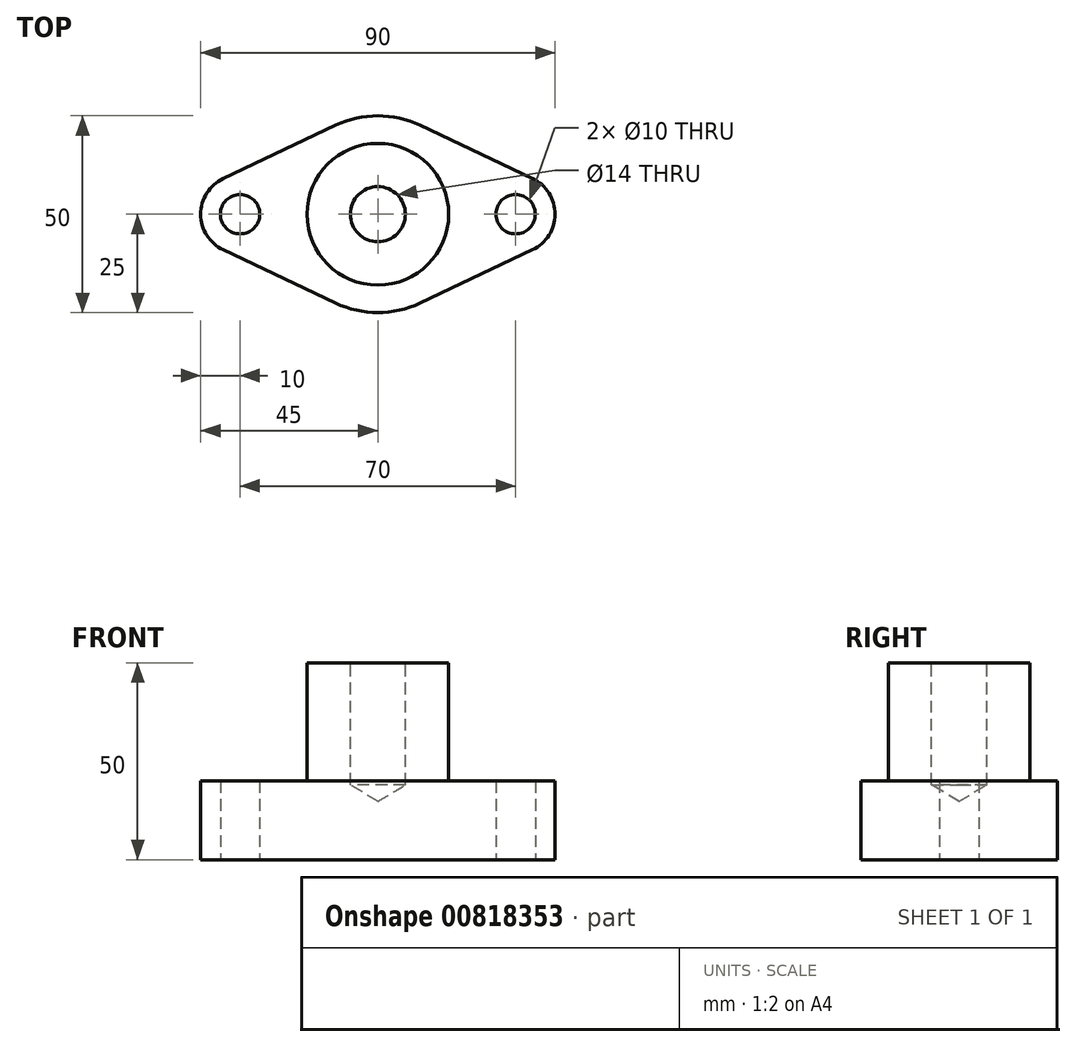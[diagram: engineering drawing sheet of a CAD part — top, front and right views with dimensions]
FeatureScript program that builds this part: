
annotation { "Feature Type Name" : "Feature", "Feature Type Description" : "" }
export const myFeature = defineFeature(function(context is Context, id is Id, definition is map)
    precondition{}
    {
        {
            var Q0;
            Q0=qCreatedBy(makeId("Top.planeOp"),FACE);
            var sketch = newSketch(context, id + "F0", { "sketchPlane" : qUnion([Q0])});
            skLineSegment(sketch, "E0", {"start": v(10.71, 22.59) * mm, "end": v(39.29, 9.04) * mm});
            skLineSegment(sketch, "E1", {"start": v(-39.29, 9.04) * mm, "end": v(-10.71, 22.59) * mm});
            skLineSegment(sketch, "E2", {"start": v(-39.29, -9.04) * mm, "end": v(-10.71, -22.59) * mm});
            skLineSegment(sketch, "E3", {"start": v(10.71, -22.59) * mm, "end": v(39.29, -9.04) * mm});
            skLineSegment(sketch, "E4", {"start": v(-10.71, 22.59) * mm, "end": v(-10.71, 22.59) * mm});
            skArc(sketch, "E5", {"start": v(-10.71, -22.59) * mm, "mid": v(0, -25) * mm, "end": v(10.71, -22.59) * mm});
            skArc(sketch, "E6", {"start": v(10.71, 22.59) * mm, "mid": v(0, 25) * mm, "end": v(-10.71, 22.59) * mm});
            skArc(sketch, "E7", {"start": v(-39.29, 9.04) * mm, "mid": v(-45, 0) * mm, "end": v(-39.29, -9.04) * mm});
            skArc(sketch, "E8", {"start": v(39.29, -9.04) * mm, "mid": v(45, 0) * mm, "end": v(39.29, 9.04) * mm});
            skSolve(sketch);
        }
        {
            var Q0;
            Q0=makeQuery(id+"F0.imprint","IMPRINT",FACE,{"disambiguationData":[TD([[makeQuery(id+"F0.imprint","IMPRINT",EDGE,{"derivedFrom":sQuery(id+"F0.wireOp",EDGE,"E0")}),-1.0]])]});
            extrude(context, id + "F1", {"entities" : qUnion([Q0]), "depth" : 20 * mm, "offsetDistance" : 25 * mm});
        }
        {
            var Q0;
            Q0=sQuery(id+"F0.wireOp",VERTEX,"E7.center");
            var Q1;
            Q1=sQuery(id+"F0.wireOp",VERTEX,"E8.center");
            var Q2;
            Q2=makeQuery(id+"F1.opExtrude","SWEPT_BODY",BODY,{"disambiguationData":[OSD([sQuery(id+"F0.wireOp",EDGE,"E0"),sQuery(id+"F0.wireOp",EDGE,"E1"),sQuery(id+"F0.wireOp",EDGE,"E2"),sQuery(id+"F0.wireOp",EDGE,"E3"),sQuery(id+"F0.wireOp",EDGE,"E5"),sQuery(id+"F0.wireOp",EDGE,"E6"),sQuery(id+"F0.wireOp",EDGE,"E7"),sQuery(id+"F0.wireOp",EDGE,"E8")])]});
            hole(context, id + "F2", {"style" : HoleStyle.SIMPLE, "endStyle" : HoleEndStyle.THROUGH, "oppositeDirection" : true, "holeDiameter" : 10 * mm, "majorDiameter" : 5 * mm, "isTappedThrough" : true, "tappedDepth" : 12 * mm, "tapClearance" : 3, "startFromSketch" : true, "locations" : qUnion([Q0, Q1]), "scope" : qUnion([Q2])});
        }
        {
            var Q0;
            Q0=makeQuery(id+"F1.opExtrude","CAP_FACE",FACE,{"disambiguationData":[OSD([sQuery(id+"F0.wireOp",EDGE,"E0"),sQuery(id+"F0.wireOp",EDGE,"E1"),sQuery(id+"F0.wireOp",EDGE,"E2"),sQuery(id+"F0.wireOp",EDGE,"E3"),sQuery(id+"F0.wireOp",EDGE,"E5"),sQuery(id+"F0.wireOp",EDGE,"E6"),sQuery(id+"F0.wireOp",EDGE,"E7"),sQuery(id+"F0.wireOp",EDGE,"E8")])],"isStart":false});
            var sketch = newSketch(context, id + "F3", { "sketchPlane" : qUnion([Q0])});
            skCircle(sketch, "E9", {"center": v(0, 0) * mm, "radius": 18 * mm});
            skSolve(sketch);
        }
        {
            var Q0;
            Q0=makeQuery(id+"F3.imprint","IMPRINT",FACE,{"disambiguationData":[TD([[makeQuery(id+"F3.imprint","IMPRINT",EDGE,{"derivedFrom":sQuery(id+"F3.wireOp",EDGE,"E9")}),1.0]])]});
            extrude(context, id + "F4", {"entities" : qUnion([Q0]), "operationType" : NewBodyOperationType.ADD, "depth" : 30 * mm, "offsetDistance" : 25 * mm});
        }
        {
            var Q0;
            Q0=makeQuery(id+"F4.opExtrude","CAP_FACE",FACE,{"disambiguationData":[OSD([sQuery(id+"F3.wireOp",EDGE,"E9")])],"isStart":false});
            var sketch = newSketch(context, id + "F5", { "sketchPlane" : qUnion([Q0])});
            skPoint(sketch, "E10", {"position": v(0, 0) * mm});
            skSolve(sketch);
        }
        {
            var Q0;
            Q0=sQuery(id+"F5.wireOp",VERTEX,"E10");
            var Q1;
            Q1=makeQuery(id+"F1.opExtrude","SWEPT_BODY",BODY,{"disambiguationData":[OSD([sQuery(id+"F0.wireOp",EDGE,"E0"),sQuery(id+"F0.wireOp",EDGE,"E1"),sQuery(id+"F0.wireOp",EDGE,"E2"),sQuery(id+"F0.wireOp",EDGE,"E3"),sQuery(id+"F0.wireOp",EDGE,"E5"),sQuery(id+"F0.wireOp",EDGE,"E6"),sQuery(id+"F0.wireOp",EDGE,"E7"),sQuery(id+"F0.wireOp",EDGE,"E8")])]});
            hole(context, id + "F6", {"style" : HoleStyle.SIMPLE, "endStyle" : HoleEndStyle.BLIND, "standardTappedOrClearance" : lookupTablePath({ "standard" : "ISO", "engagement" : "75%", "pitch" : "2 mm", "size" : "M16", "type" : "Tapped" }), "standardBlindInLast" : lookupTablePath({ "standard" : "ISO", "engagement" : "75%", "pitch" : "2 mm", "size" : "M16", "type" : "Tapped" }), "holeDiameter" : 14 * mm, "majorDiameter" : 16 * mm, "showTappedDepth" : true, "holeDepth" : 31 * mm, "isTappedThrough" : true, "tappedDepth" : 25 * mm, "tapClearance" : 3, "startFromSketch" : true, "locations" : qUnion([Q0]), "scope" : qUnion([Q1])});
        }
    });
